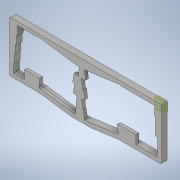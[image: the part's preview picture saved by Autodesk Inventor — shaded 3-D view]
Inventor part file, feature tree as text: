
AUTODESK INVENTOR PART (.ipt)
format: ipt  version: 2022 (Build 260153000, 153)  size: 381,440 bytes
history: native  units: in
note: dims shown in document units (in); Inventor stores cm internally (conversion verified against a paired STEP export)
features: extrude x4, plane x2, fillet x2, sketch x2
ambient origin geometry x8: Origin, YZ Plane, XZ Plane, XY Plane, X Axis, Y Axis, Z Axis, Center Point
bodies: Body1 (feature_tree)
feature tree (10):
  plane  "Work Plane1"
  extrude  "Extrusion1"  Depth=0.1181in
  plane  "Work Plane4"
  fillet  "Fillet3"  Radius=0.1181in
  extrude  "Extrusion4"  Depth=0.2283in
  fillet  "Fillet2"  Radius=0.1181in
  extrude  "Extrusion5"  Depth=0.2283in
  extrude  "Extrusion6"  Depth=0.2283in
  sketch  "Sketch1"  dims[d1=0.1181in d2=0.1181in d3=0.1181in]
  sketch  "Sketch3"  dims[d4=0.1181in d5=0.1181in d7=0.1181in d8=0.6181in d9=0.1181in d10=0.1181in d11=0.1181in d12=0.1181in d13=0.1181in d14=0.1181in d15=13.0469in d16=0.25in d17=0.0in d18=0.0787in d19=0.0197in d39=0.25in d40=0.1181in d41=0.1181in d42=0.1181in d43=0.1181in d44=0.1181in d45=0.1181in d46=0.6181in d47=0.1181in d48=0.1181in d49=0.1181in d50=0.1181in d51=0.1181in d52=0.1181in d53=13.0469in d54=0.25in d55=0.0in d59=0.2756in d60=0.2756in d61=0.1555in d62=0.2756in d63=0.2756in d64=0.1555in d65=0.2756in d66=0.2756in d67=0.2756in d68=0.2756in d69=0.1555in d70=0.1555in d71=2.625in d72=0.0in d73=0.2283in d74=0.0in]
